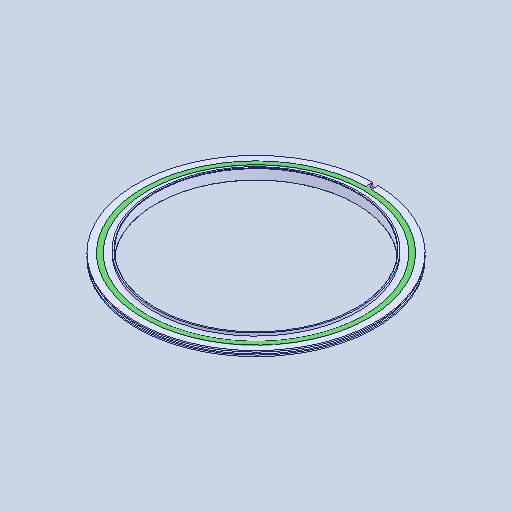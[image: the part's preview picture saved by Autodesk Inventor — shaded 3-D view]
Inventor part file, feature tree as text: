
AUTODESK INVENTOR PART (.ipt)
format: ipt  version: 2023 (Build 270158000, 158)  size: 215,552 bytes
history: native  units: in
note: dims shown in document units (in); Inventor stores cm internally (conversion verified against a paired STEP export)
features: revolve x2, chamfer x1, other x1
ambient origin geometry x8: Origin, YZ Plane, XZ Plane, XY Plane, X Axis, Y Axis, Z Axis, Center Point
bodies: Solid1 (feature_tree), Solid2 (feature_tree), Solid3 (feature_tree), Solid4 (feature_tree)
feature tree (4):
  chamfer  "Chamfer1"  [1 undecoded]
  revolve  "Revolve2"  [1 undecoded]
  other  "Cut-Extrude1"
  revolve  "Revolve4"  [1 undecoded]
note: 3 required parameter values undecoded (feature->parameter linkage not recoverable at this tier; creation-order binding heuristic only, values carry confidence <= 0.55)
